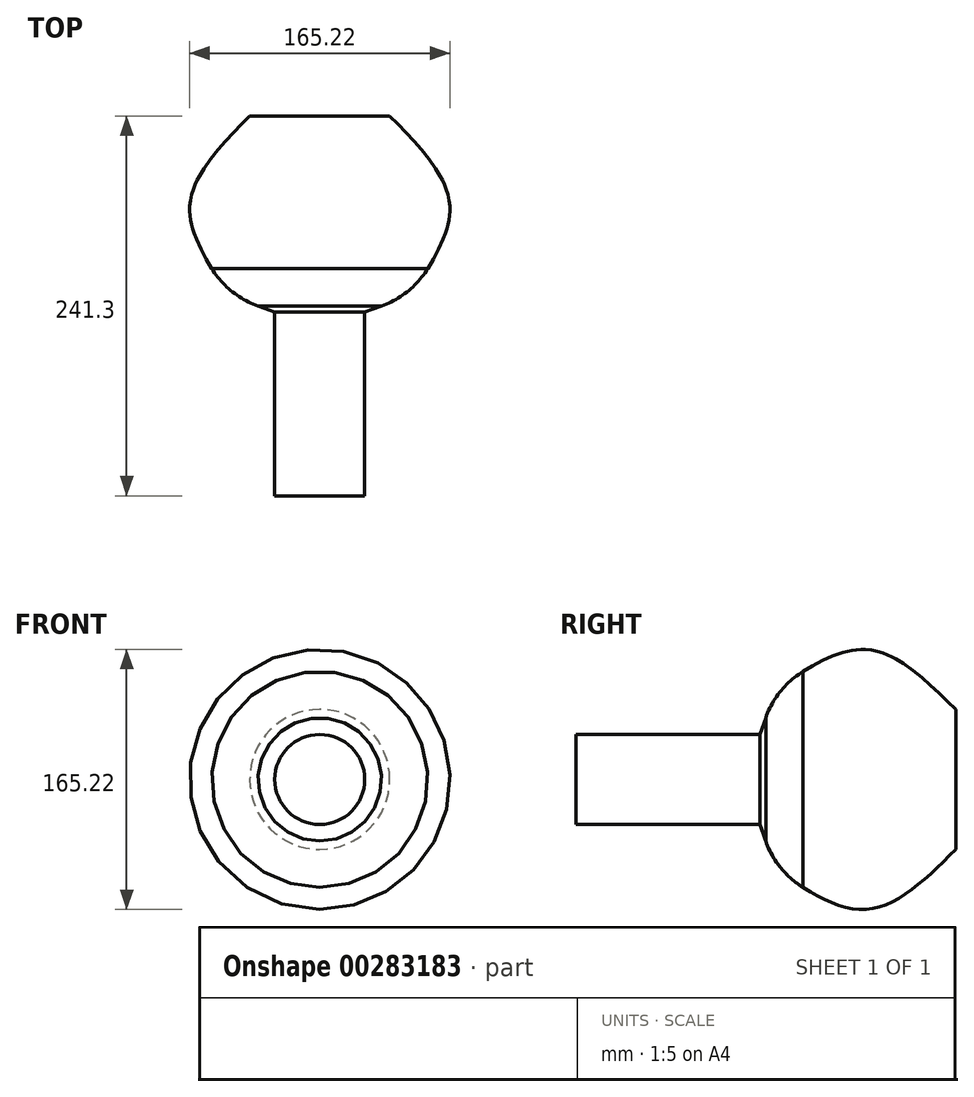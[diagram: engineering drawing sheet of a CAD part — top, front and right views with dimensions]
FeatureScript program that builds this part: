
annotation { "Feature Type Name" : "Feature", "Feature Type Description" : "" }
export const myFeature = defineFeature(function(context is Context, id is Id, definition is map)
    precondition{}
    {
        {
            var Q0;
            Q0=qCreatedBy(makeId("Front.planeOp"),FACE);
            var sketch = newSketch(context, id + "F0", { "sketchPlane" : qUnion([Q0])});
            skCircle(sketch, "E0", {"center": v(0, 0) * mm, "radius": 44.45 * mm});
            skSolve(sketch);
        }
        {
            var Q0;
            Q0=qCreatedBy(makeId("Front.planeOp"),FACE);
            cPlane(context, id + "F1", {"entities" : qUnion([Q0]), "cplaneType" : CPlaneType.OFFSET, "offset" : 57.15 * mm, "width" : 152.4 * mm, "height" : 152.4 * mm});
        }
        {
            var Q0;
            Q0=qCreatedBy(id+"F1.planeOp",FACE);
            var sketch = newSketch(context, id + "F2", { "sketchPlane" : qUnion([Q0])});
            skCircle(sketch, "E1", {"center": v(0, 0) * mm, "radius": 82.55 * mm});
            skSolve(sketch);
        }
        {
            var Q0;
            Q0=qCreatedBy(id+"F1.planeOp",FACE);
            cPlane(context, id + "F3", {"entities" : qUnion([Q0]), "cplaneType" : CPlaneType.OFFSET, "offset" : 57.15 * mm, "width" : 152.4 * mm, "height" : 152.4 * mm});
        }
        {
            var Q0;
            Q0=qCreatedBy(id+"F3.planeOp",FACE);
            var sketch = newSketch(context, id + "F4", { "sketchPlane" : qUnion([Q0])});
            skCircle(sketch, "E2", {"center": v(0, 0) * mm, "radius": 57.15 * mm});
            skSolve(sketch);
        }
        {
            var Q0;
            Q0=qCreatedBy(id+"F3.planeOp",FACE);
            cPlane(context, id + "F5", {"entities" : qUnion([Q0]), "cplaneType" : CPlaneType.OFFSET, "offset" : 127 * mm, "width" : 152.4 * mm, "height" : 152.4 * mm});
        }
        {
            var Q0;
            Q0=makeQuery(id+"F0.imprint","IMPRINT",FACE,{"disambiguationData":[TD([[makeQuery(id+"F0.imprint","IMPRINT",EDGE,{"derivedFrom":sQuery(id+"F0.wireOp",EDGE,"E0")}),1.0]])]});
            var Q1;
            Q1=makeQuery(id+"F2.imprint","IMPRINT",FACE,{"disambiguationData":[TD([[makeQuery(id+"F2.imprint","IMPRINT",EDGE,{"derivedFrom":sQuery(id+"F2.wireOp",EDGE,"E1")}),1.0]])]});
            var Q2;
            Q2=makeQuery(id+"F4.imprint","IMPRINT",FACE,{"disambiguationData":[TD([[makeQuery(id+"F4.imprint","IMPRINT",EDGE,{"derivedFrom":sQuery(id+"F4.wireOp",EDGE,"E2")}),1.0]])]});
            loft(context, id + "F6", {"sheetProfilesArray" : [{ "sheetProfileEntities" : qUnion([Q0]) }, { "sheetProfileEntities" : qUnion([Q1]) }, { "sheetProfileEntities" : qUnion([Q2]) }]});
        }
        {
            var Q0;
            Q0=qCreatedBy(id+"F3.planeOp",FACE);
            cPlane(context, id + "F7", {"entities" : qUnion([Q0]), "cplaneType" : CPlaneType.OFFSET, "offset" : 10.16 * mm, "width" : 152.4 * mm, "height" : 152.4 * mm});
        }
        {
            var Q0;
            Q0=qCreatedBy(id+"F7.planeOp",FACE);
            var sketch = newSketch(context, id + "F8", { "sketchPlane" : qUnion([Q0])});
            skCircle(sketch, "E3", {"center": v(0, 0) * mm, "radius": 28.58 * mm});
            skSolve(sketch);
        }
        {
            var Q0;
            Q0=qCreatedBy(id+"F5.planeOp",FACE);
            var sketch = newSketch(context, id + "F9", { "sketchPlane" : qUnion([Q0])});
            skCircle(sketch, "E4", {"center": v(0, 0) * mm, "radius": 28.58 * mm});
            skSolve(sketch);
        }
        {
            var Q1;
            Q1=makeQuery(id+"F6.opLoft","CAP_FACE",FACE,{"disambiguationData":[OSD([makeQuery(id+"F4.imprint","IMPRINT",FACE,{"disambiguationData":[TD([[makeQuery(id+"F4.imprint","IMPRINT",EDGE,{"derivedFrom":sQuery(id+"F4.wireOp",EDGE,"E2")}),1.0]])]})])],"isStart":true});
            var Q2;
            Q2=makeQuery(id+"F8.imprint","IMPRINT",FACE,{"disambiguationData":[TD([[makeQuery(id+"F8.imprint","IMPRINT",EDGE,{"derivedFrom":sQuery(id+"F8.wireOp",EDGE,"E3")}),1.0]])]});
            loft(context, id + "F10", {"operationType" : NewBodyOperationType.ADD, "sheetProfilesArray" : [{ "sheetProfileEntities" : qUnion([Q1]) }, { "sheetProfileEntities" : qUnion([Q2]) }]});
        }
        {
            var Q1;
            Q1=makeQuery(id+"F10.opLoft","CAP_FACE",FACE,{"disambiguationData":[OSD([makeQuery(id+"F8.imprint","IMPRINT",FACE,{"disambiguationData":[TD([[makeQuery(id+"F8.imprint","IMPRINT",EDGE,{"derivedFrom":sQuery(id+"F8.wireOp",EDGE,"E3")}),1.0]])]})])],"isStart":true});
            var Q2;
            Q2=makeQuery(id+"F9.imprint","IMPRINT",FACE,{"disambiguationData":[TD([[makeQuery(id+"F9.imprint","IMPRINT",EDGE,{"derivedFrom":sQuery(id+"F9.wireOp",EDGE,"E4")}),1.0]])]});
            loft(context, id + "F11", {"operationType" : NewBodyOperationType.ADD, "sheetProfilesArray" : [{ "sheetProfileEntities" : qUnion([Q1]) }, { "sheetProfileEntities" : qUnion([Q2]) }]});
        }
        {
            var Q0;
            {var subQ0=sQuery(id+"F4.wireOp",EDGE,"E2");var subQ1=sQuery(id+"F0.wireOp",EDGE,"E0");Q0=makeQuery(id+"F10.boolean.opBoolean","MERGE",EDGE,{"derivedFrom":[makeQuery(id+"F6.opLoft","MID_CAP_EDGE",EDGE,{"disambiguationData":[OSD([subQ1,subQ0])],"capPos":2.0}),makeQuery(id+"F10.opLoft","MID_CAP_EDGE",EDGE,{"disambiguationData":[OSD([subQ1,subQ0])],"capPos":0.0})]});}
            fillet(context, id + "F12", {"entities" : qUnion([Q0]), "radius" : 57.15 * mm, "tangentPropagation" : true, "allowEdgeOverflow" : false});
        }
    });
